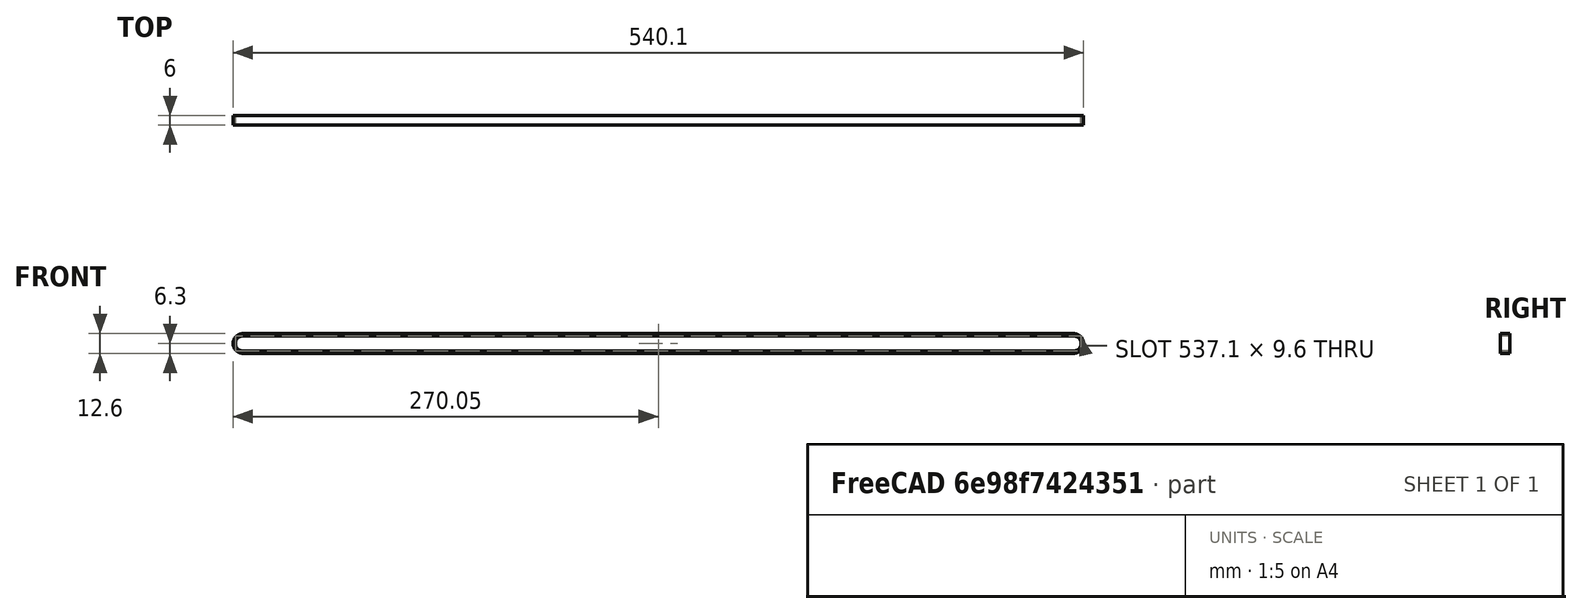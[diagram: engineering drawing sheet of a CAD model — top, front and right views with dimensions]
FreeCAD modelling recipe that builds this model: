
FCSTD DOCUMENT  (FreeCAD 0.18R14555 (Git shallow))
Label: x-gt2-belt
License: All rights reserved
LicenseURL: http://en.wikipedia.org/wiki/All_rights_reserved
objects: Sketcher::SketchObject×1, PartDesign::Pad×1, PartDesign::Body×1
note: 4 computed .brp shape members not serialized (recipe doc carries the construction recipe); baked Part::Feature solids carry a one-line shape summary decoded from their .brp

FEATURE [Sketcher::SketchObject] Sketch
  MapMode = 5
  Placement = pos=(0,0,0) rot=(1,0,0;1.5708rad)
  Support = -> [XZ_Plane]
  sketch-geometry (10):
    g0: ArcOfCircle CenterX=-263.75 CenterY=0 CenterZ=0 NormalX=0 NormalY=0 NormalZ=1 AngleXU=0 Radius=4.8 StartAngle=1.5708 EndAngle=4.71239
    g1: ArcOfCircle CenterX=263.75 CenterY=-3e-16 CenterZ=0 NormalX=0 NormalY=0 NormalZ=1 AngleXU=0 Radius=4.8 StartAngle=4.71239 EndAngle=7.85398
    g2: ArcOfCircle CenterX=-263.75 CenterY=0 CenterZ=0 NormalX=0 NormalY=0 NormalZ=1 AngleXU=0 Radius=6.3 StartAngle=1.5708 EndAngle=4.71239
    g3: ArcOfCircle CenterX=263.75 CenterY=-3e-16 CenterZ=0 NormalX=0 NormalY=0 NormalZ=1 AngleXU=0 Radius=6.3 StartAngle=4.71239 EndAngle=7.85398
    g4: LineSegment StartX=-263.75 StartY=6.3 StartZ=0 EndX=263.75 EndY=6.3 EndZ=0
    g5: LineSegment StartX=263.75 StartY=4.8 StartZ=0 EndX=-263.75 EndY=4.8 EndZ=0
    g6: LineSegment StartX=-263.75 StartY=-4.8 StartZ=0 EndX=263.75 EndY=-4.8 EndZ=0
    g7: LineSegment StartX=263.75 StartY=-6.3 StartZ=0 EndX=-263.75 EndY=-6.3 EndZ=0
    g8: LineSegment [constr] StartX=-263.75 StartY=4.8 StartZ=0 EndX=0 EndY=0 EndZ=0
    g9: LineSegment [constr] StartX=0 StartY=0 StartZ=0 EndX=263.75 EndY=4.8 EndZ=0
  constraints (23):
    c: Coincident(g2,g0)
    c: Coincident(g3,g1)
    c: Horizontal(g4)
    c: Horizontal(g5)
    c: Coincident(g6,g1)
    c: Horizontal(g6)
    c: Tangent(g6,g1)
    c: Tangent(g7,g3) = 1.5708
    c: Tangent(g5,g1) = -1.5708
    c: Tangent(g4,g3) = 1.5708
    c: Tangent(g4,g2) = 1.5708
    c: Tangent(g5,g0) = -1.5708
    c: Tangent(g6,g0) = -1.5708
    c: Tangent(g7,g2) = 1.5708
    c: DistanceY(g0,g2) = 1.5
    c: Radius(g0) = 4.8
    c: Coincident(g8,g0)
    c: Coincident(g8,g-1)
    c: Coincident(g9,g-1)
    c: Coincident(g9,g1)
    c: Equal(g8,g9)
    c: PointOnObject(g0,g-1)
    c: DistanceX(g0,g1) = 527.5
FEATURE [PartDesign::Pad] Pad
  Length = 6
  Length2 = 100
  Placement = pos=(0,0,0) rot=(1,0,0;1.5708rad)
  Profile = -> Sketch
  Type = 0
FEATURE [PartDesign::Body] Body
  Group = -> [Sketch,Pad]
  Origin = -> Origin
  Tip = -> Pad
